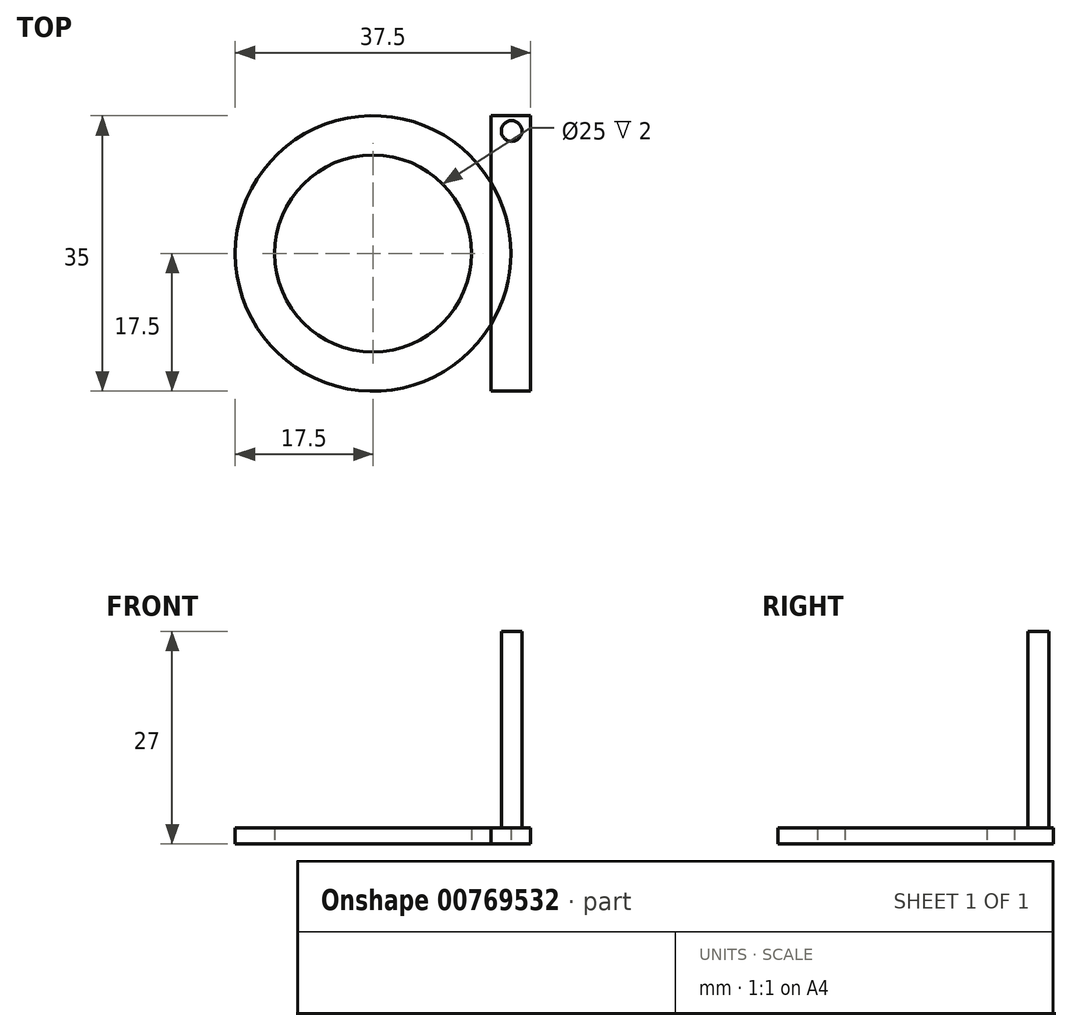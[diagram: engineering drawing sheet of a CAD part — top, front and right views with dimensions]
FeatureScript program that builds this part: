
annotation { "Feature Type Name" : "Feature", "Feature Type Description" : "" }
export const myFeature = defineFeature(function(context is Context, id is Id, definition is map)
    precondition{}
    {
        {
            var Q0;
            Q0=qCreatedBy(makeId("Top.planeOp"),FACE);
            var sketch = newSketch(context, id + "F0", { "sketchPlane" : qUnion([Q0])});
            skCircle(sketch, "E0", {"center": v(0, 0) * mm, "radius": 17.5 * mm});
            skCircle(sketch, "E1", {"center": v(0, 0) * mm, "radius": 12.5 * mm});
            skLineSegment(sketch, "E2.bottom", {"start": v(15, 17.5) * mm, "end": v(20, 17.5) * mm});
            skLineSegment(sketch, "E2.top", {"start": v(15, -17.5) * mm, "end": v(20, -17.5) * mm});
            skLineSegment(sketch, "E2.left", {"start": v(15, 17.5) * mm, "end": v(15, -17.5) * mm});
            skLineSegment(sketch, "E2.right", {"start": v(20, 17.5) * mm, "end": v(20, -17.5) * mm});
            skSolve(sketch);
        }
        {
            var Q0;
            {var subQ0=sQuery(id+"F0.wireOp",EDGE,"E2.left");var subQ1=sQuery(id+"F0.wireOp",EDGE,"E0");var subQ2=makeQuery(id+"F0.imprint","INTERSECT",VERTEX,{"disambiguationData":[OD(0.0)],"derivedFrom":[subQ1,subQ0]});Q0=makeQuery(id+"F0.imprint","IMPRINT",FACE,{"disambiguationData":[TD([[makeQuery(id+"F0.imprint","IMPRINT",EDGE,{"disambiguationData":[TD([[subQ2,1.0]])],"derivedFrom":subQ1}),1.0]])]});}
            var Q1;
            {var subQ1=sQuery(id+"F0.wireOp",EDGE,"E2.bottom");Q1=makeQuery(id+"F0.imprint","IMPRINT",FACE,{"disambiguationData":[TD([[makeQuery(id+"F0.imprint","IMPRINT",EDGE,{"derivedFrom":subQ1}),-1.0]])]});}
            var Q2;
            Q2=makeQuery(id+"F0.imprint","IMPRINT",FACE,{"disambiguationData":[TD([[makeQuery(id+"F0.imprint","IMPRINT",EDGE,{"derivedFrom":sQuery(id+"F0.wireOp",EDGE,"E1")}),-1.0]])]});
            extrude(context, id + "F1", {"entities" : qUnion([Q0, Q1, Q2]), "depth" : 2 * mm, "offsetDistance" : 25 * mm});
        }
        {
            var Q0;
            Q0=makeQuery(id+"F1.opExtrude","CAP_FACE",FACE,{"disambiguationData":[OSD([sQuery(id+"F0.wireOp",EDGE,"E0"),sQuery(id+"F0.wireOp",EDGE,"E1"),sQuery(id+"F0.wireOp",EDGE,"E2.bottom"),sQuery(id+"F0.wireOp",EDGE,"E2.top"),sQuery(id+"F0.wireOp",EDGE,"E2.left"),sQuery(id+"F0.wireOp",EDGE,"E2.right")])],"isStart":false});
            var sketch = newSketch(context, id + "F2", { "sketchPlane" : qUnion([Q0])});
            skCircle(sketch, "E3", {"center": v(17.61, 15.56) * mm, "radius": 1.32 * mm});
            skSolve(sketch);
        }
        {
            var Q0;
            Q0=makeQuery(id+"F2.imprint","IMPRINT",FACE,{"disambiguationData":[TD([[makeQuery(id+"F2.imprint","IMPRINT",EDGE,{"derivedFrom":sQuery(id+"F2.wireOp",EDGE,"E3")}),1.0]])]});
            extrude(context, id + "F3", {"entities" : qUnion([Q0]), "operationType" : NewBodyOperationType.ADD, "depth" : 25 * mm, "offsetDistance" : 25 * mm});
        }
    });
